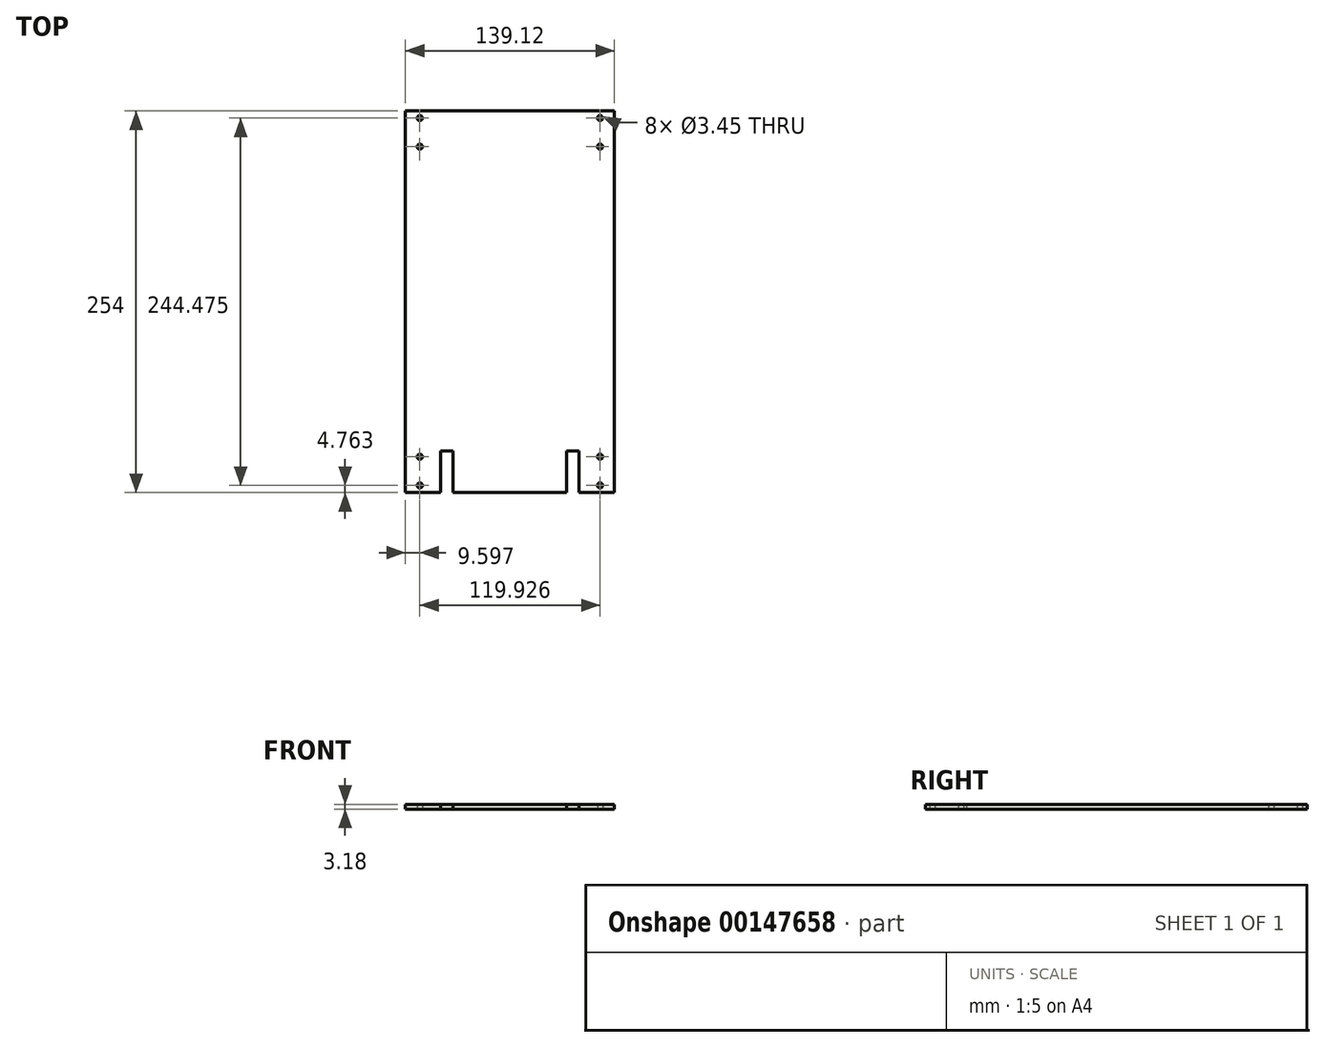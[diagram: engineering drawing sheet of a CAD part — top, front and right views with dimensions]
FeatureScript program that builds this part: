
annotation { "Feature Type Name" : "Feature", "Feature Type Description" : "" }
export const myFeature = defineFeature(function(context is Context, id is Id, definition is map)
    precondition{}
    {
        {
            var Q0;
            Q0=qCreatedBy(makeId("Top.planeOp"),FACE);
            var sketch = newSketch(context, id + "F0", { "sketchPlane" : qUnion([Q0])});
            skLineSegment(sketch, "E0.bottom", {"start": v(69.56, -127) * mm, "end": v(-69.56, -127) * mm});
            skLineSegment(sketch, "E0.top", {"start": v(69.56, 127) * mm, "end": v(-69.56, 127) * mm});
            skLineSegment(sketch, "E0.left", {"start": v(69.56, -127) * mm, "end": v(69.56, 127) * mm});
            skLineSegment(sketch, "E0.right", {"start": v(-69.56, -127) * mm, "end": v(-69.56, 127) * mm});
            skPoint(sketch, "E0.middle", {"position": v(0, 0) * mm});
            skLineSegment(sketch, "E1", {"start": v(59.96, 103.19) * mm, "end": v(69.56, 103.19) * mm, "construction": true});
            skLineSegment(sketch, "E2.bottom", {"start": v(59.96, 103.19) * mm, "end": v(-59.96, 103.19) * mm, "construction": true});
            skLineSegment(sketch, "E2.top", {"start": v(59.96, -103.19) * mm, "end": v(-59.96, -103.19) * mm, "construction": true});
            skLineSegment(sketch, "E2.left", {"start": v(59.96, 103.19) * mm, "end": v(59.96, -103.19) * mm, "construction": true});
            skLineSegment(sketch, "E2.right", {"start": v(-59.96, 103.19) * mm, "end": v(-59.96, -103.19) * mm, "construction": true});
            skCircle(sketch, "E3", {"center": v(59.96, 103.19) * mm, "radius": 1.73 * mm});
            skCircle(sketch, "E4", {"center": v(-59.96, -103.19) * mm, "radius": 1.73 * mm});
            skLineSegment(sketch, "E5", {"start": v(0, 103.19) * mm, "end": v(0, 127) * mm, "construction": true});
            skLineSegment(sketch, "E6", {"start": v(59.96, 103.19) * mm, "end": v(59.96, 122.24) * mm, "construction": true});
            skCircle(sketch, "E7", {"center": v(-59.96, 103.19) * mm, "radius": 1.73 * mm});
            skCircle(sketch, "E8", {"center": v(59.96, -103.19) * mm, "radius": 1.73 * mm});
            skLineSegment(sketch, "E9", {"start": v(59.96, 122.24) * mm, "end": v(59.96, 127) * mm, "construction": true});
            skCircle(sketch, "E10", {"center": v(59.96, 122.24) * mm, "radius": 1.73 * mm});
            skLineSegment(sketch, "E11", {"start": v(-59.96, 103.19) * mm, "end": v(-59.96, 122.24) * mm, "construction": true});
            skLineSegment(sketch, "E12", {"start": v(-59.96, 122.24) * mm, "end": v(-59.96, 127) * mm, "construction": true});
            skLineSegment(sketch, "E13", {"start": v(-59.96, -103.19) * mm, "end": v(-59.96, -122.24) * mm, "construction": true});
            skLineSegment(sketch, "E14", {"start": v(-59.96, -122.24) * mm, "end": v(-59.96, -127) * mm, "construction": true});
            skLineSegment(sketch, "E15", {"start": v(59.96, -103.19) * mm, "end": v(59.96, -122.24) * mm, "construction": true});
            skLineSegment(sketch, "E16", {"start": v(59.96, -122.24) * mm, "end": v(59.96, -127) * mm, "construction": true});
            skCircle(sketch, "E17", {"center": v(-59.96, 122.24) * mm, "radius": 1.73 * mm});
            skCircle(sketch, "E18", {"center": v(-59.96, -122.24) * mm, "radius": 1.73 * mm});
            skCircle(sketch, "E19", {"center": v(59.96, -122.24) * mm, "radius": 1.73 * mm});
            skSolve(sketch);
        }
        {
            var Q0;
            Q0=makeQuery(id+"F0.imprint","IMPRINT",FACE,{"disambiguationData":[TD([[makeQuery(id+"F0.imprint","IMPRINT",EDGE,{"derivedFrom":sQuery(id+"F0.wireOp",EDGE,"E0.bottom")}),-1.0]])]});
            extrude(context, id + "F1", {"entities" : qUnion([Q0]), "depth" : 3.17 * mm});
        }
        {
            var Q0;
            Q0=makeQuery(id+"F1.opExtrude","CAP_FACE",FACE,{"disambiguationData":[OSD([sQuery(id+"F0.wireOp",EDGE,"E0.bottom"),sQuery(id+"F0.wireOp",EDGE,"E0.top"),sQuery(id+"F0.wireOp",EDGE,"E0.left"),sQuery(id+"F0.wireOp",EDGE,"E0.right"),sQuery(id+"F0.wireOp",EDGE,"E3"),sQuery(id+"F0.wireOp",EDGE,"E4"),sQuery(id+"F0.wireOp",EDGE,"E7"),sQuery(id+"F0.wireOp",EDGE,"E8"),sQuery(id+"F0.wireOp",EDGE,"E10"),sQuery(id+"F0.wireOp",EDGE,"E17"),sQuery(id+"F0.wireOp",EDGE,"E18"),sQuery(id+"F0.wireOp",EDGE,"E19")])],"isStart":false});
            var sketch = newSketch(context, id + "F2", { "sketchPlane" : qUnion([Q0])});
            skLineSegment(sketch, "E20.bottom", {"start": v(-46.07, -127) * mm, "end": v(-37.81, -127) * mm});
            skLineSegment(sketch, "E20.top", {"start": v(-46.07, -99.25) * mm, "end": v(-37.81, -99.25) * mm});
            skLineSegment(sketch, "E20.left", {"start": v(-46.07, -127) * mm, "end": v(-46.07, -99.25) * mm});
            skLineSegment(sketch, "E20.right", {"start": v(-37.81, -127) * mm, "end": v(-37.81, -99.25) * mm});
            skLineSegment(sketch, "E21.bottom", {"start": v(37.81, -127) * mm, "end": v(46.07, -127) * mm});
            skLineSegment(sketch, "E21.top", {"start": v(37.81, -99.25) * mm, "end": v(46.07, -99.25) * mm});
            skLineSegment(sketch, "E21.left", {"start": v(37.81, -127) * mm, "end": v(37.81, -99.25) * mm});
            skLineSegment(sketch, "E21.right", {"start": v(46.07, -127) * mm, "end": v(46.07, -99.25) * mm});
            skPoint(sketch, "E22", {"position": v(41.94, -127) * mm});
            skPoint(sketch, "E23", {"position": v(-41.94, -127) * mm});
            skLineSegment(sketch, "E24", {"start": v(46.07, -99.25) * mm, "end": v(69.56, -99.25) * mm, "construction": true});
            skLineSegment(sketch, "E25", {"start": v(-46.07, -99.25) * mm, "end": v(-69.56, -99.25) * mm, "construction": true});
            skSolve(sketch);
        }
        {
            var Q0;
            Q0=qSketchRegion(id+"F2",true);
            var Q1;
            Q1=makeQuery(id+"F1.opExtrude","CAP_FACE",FACE,{"disambiguationData":[OSD([sQuery(id+"F0.wireOp",EDGE,"E0.bottom"),sQuery(id+"F0.wireOp",EDGE,"E0.top"),sQuery(id+"F0.wireOp",EDGE,"E0.left"),sQuery(id+"F0.wireOp",EDGE,"E0.right"),sQuery(id+"F0.wireOp",EDGE,"E3"),sQuery(id+"F0.wireOp",EDGE,"E4"),sQuery(id+"F0.wireOp",EDGE,"E7"),sQuery(id+"F0.wireOp",EDGE,"E8"),sQuery(id+"F0.wireOp",EDGE,"E10"),sQuery(id+"F0.wireOp",EDGE,"E17"),sQuery(id+"F0.wireOp",EDGE,"E18"),sQuery(id+"F0.wireOp",EDGE,"E19")])],"isStart":true});
            extrude(context, id + "F3", {"entities" : qUnion([Q0]), "operationType" : NewBodyOperationType.REMOVE, "endBound" : BoundingType.UP_TO_SURFACE, "oppositeDirection" : true, "endBoundEntityFace" : qUnion([Q1]), "depth" : 25.4 * mm});
        }
    });
